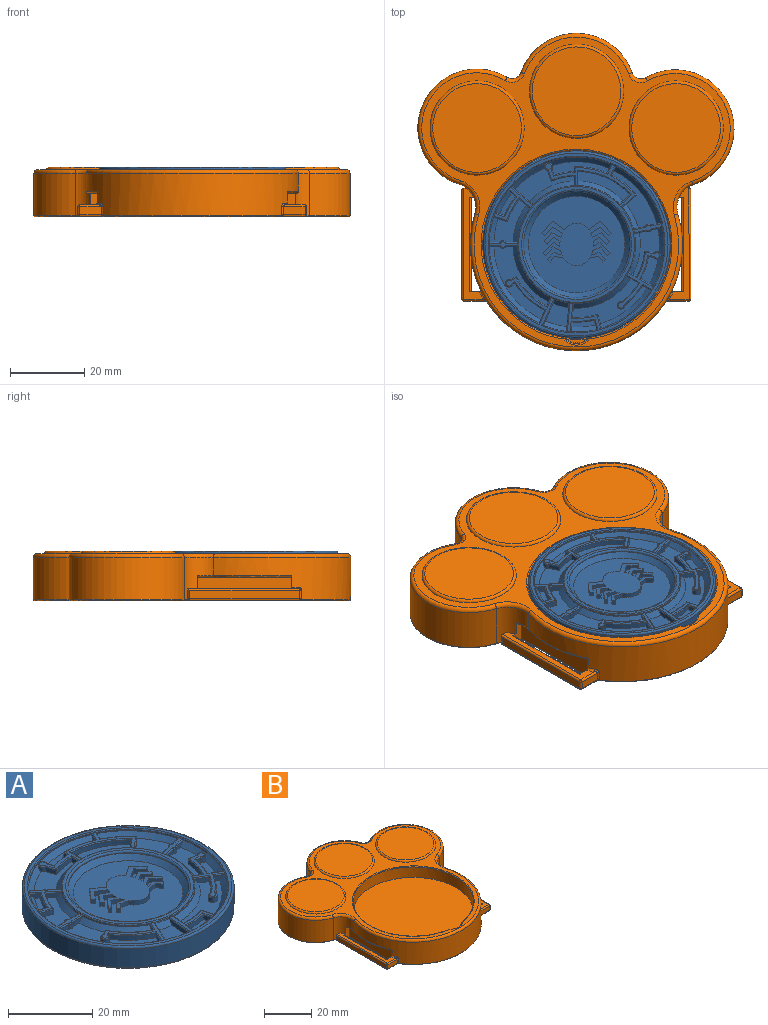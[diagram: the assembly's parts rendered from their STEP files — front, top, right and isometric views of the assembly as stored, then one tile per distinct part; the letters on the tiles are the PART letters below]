
ASSEMBLY  parts=2 mates=1
PART A: 221 faces, bbox 54.4x54.4x6.4 mm
  f0: plane 7.35x4.62mm, normal (0,0,1), area 17.8mm2, adj f80,f81,f82,f83,f107
  f1: plane 15.54x3.59mm, normal (0,0,1), area 28.4mm2, adj f25,f26,f27,f28,f29,f30,f109
  f2: cylinder r=15.88mm len=31.75mm, axis (0,0,-1), area 35mm2, adj f21,f22,f33,f34,f35,f37,f38,f43
  f3: plane 20.12x12.27mm, normal (0,0,1), area 78.1mm2, adj f48,f49,f50,f75,f76,f77,f78,f79
  f4: plane 15.52x12.18mm, normal (0,0,1), area 55.7mm2, adj f22,f23,f24,f71,f72,f73,f99,f108
  f5: plane 19.5x14.78mm, normal (0,0,1), area 91.8mm2, adj f52,f53,f54,f55,f56,f57,f58,f64
  f6: plane 6.29x6.24mm, normal (0,0,1), area 26.9mm2, adj f44,f59,f93,f103
  f7: plane 12.99x7.16mm, normal (0,0,1), area 38mm2, adj f68,f69,f70,f83,f84,f85,f86,f98
  f8: plane 11.56x8.8mm, normal (0,0,1), area 45mm2, adj f36,f37,f42,f61,f62,f63,f95,f105
  f9: plane 6.13x4.32mm, normal (0,0,1), area 8.6mm2, adj f39,f40,f41,f106
  f10: plane 6.52x1.92mm, normal (0,0,1), area 8.6mm2, adj f45,f46,f47,f102
  f11: plane 16.01x9.07mm, normal (0,0,1), area 54.4mm2, adj f30,f31,f32,f33,f38,f96,f109
  f12: cylinder r=25.15mm len=50.29mm, axis (0,0,1), area 872.9mm2, adj f88,f171
  f13: plane 49.66x49.66mm, normal (0,0,-1), area 1936.6mm2, adj f171
  f14: cylinder r=23.58mm len=47.17mm, axis (0,0,-1), area 53.1mm2, adj f24,f25,f35,f38,f39,f41,f42,f43
  f15: plane 49.28x49.28mm, normal (0,0,1), area 121.8mm2, adj f88,f90
  f16: plane 13.76x7.93mm, normal (0,0,1), area 36.7mm2, adj f20,f21,f34,f100
  f17: cylinder r=14.29mm len=28.58mm, axis (0,0,-1), area 11.4mm2, adj f89,f92
  f18: plane 31.24x31.24mm, normal (0,0,1), area 78.9mm2, adj f89,f91
  f19: plane 26.04x26.04mm, normal (0,0,1), area 405.4mm2, adj f92,f172,f173,f174,f175,f176,f177,f178
  f20: cylinder r=19.69mm len=13.76mm, axis (0,0,-1), area 20.7mm2, adj f16,f21,f34,f111
  f21: plane 2.85x2.53mm, normal (-0.66,0.75,0), area 4.3mm2, adj f2,f16,f20,f100,f112
  f22: plane 3.83x3.35mm, normal (0.66,-0.75,0), area 6mm2, adj f2,f4,f23,f99,f115
  f23: cylinder r=20.96mm len=6.76mm, axis (0,0,-1), area 11.6mm2, adj f4,f22,f24,f114
  f24: plane 2.38x1.33mm, normal (0.91,-0.42,0), area 2.7mm2, adj f4,f14,f23,f108,f113
  f25: plane 2.39x1.33mm, normal (-0.91,0.42,0), area 2.7mm2, adj f1,f14,f26,f109,f124
  f26: cylinder r=20.96mm len=8.91mm, axis (0,0,-1), area 12.2mm2, adj f1,f25,f27,f123
  f27: plane 1.33x1.27mm, normal (-1,0,0), area 1.7mm2, adj f1,f26,f28,f122
  f28: cylinder r=19.69mm len=5.45mm, axis (0,0,-1), area 7.4mm2, adj f1,f27,f29,f121
  f29: plane 1.66x1.33mm, normal (0.94,0.34,0), area 2.4mm2, adj f1,f28,f30,f120
  f30: cylinder r=1.07mm len=2.13mm, axis (0,0,-1), area 4.9mm2, adj f1,f11,f29,f31,f109,f119
  f31: plane 2.85x1.33mm, normal (-0.94,-0.34,0), area 4mm2, adj f11,f30,f32,f118
  f32: cylinder r=18.41mm len=6.22mm, axis (0,0,-1), area 8.5mm2, adj f11,f31,f33,f117
  f33: plane 2.54x1.34mm, normal (-1,0,0), area 2.6mm2, adj f2,f11,f32,f96,f116
  f34: plane 3.81x1.34mm, normal (1,0,0), area 4.3mm2, adj f2,f16,f20,f100,f110
  f35: plane 24.22x11.62mm, normal (0,0,1), area 30.8mm2, adj f2,f14,f110,f111,f112,f113,f114,f115
  f36: cylinder r=19.69mm len=6.06mm, axis (0,0,-1), area 9.2mm2, adj f8,f37,f42,f165
  f37: plane 2.92x2.46mm, normal (-0.64,-0.77,0), area 4.3mm2, adj f2,f8,f36,f95,f166
  f38: plane 5.9x4.97mm, normal (0.64,0.76,0), area 8.7mm2, adj f2,f11,f14,f96,f109,f167
  f39: plane 2.01x1.7mm, normal (-0.64,-0.76,0), area 2.7mm2, adj f9,f14,f40,f106,f170
  f40: cylinder r=20.96mm len=5.25mm, axis (0,0,-1), area 8.1mm2, adj f9,f39,f41,f169
  f41: plane 2.47x1.33mm, normal (0.34,0.94,0), area 2.7mm2, adj f9,f14,f40,f106,f168
  f42: plane 3.67x1.34mm, normal (-0.34,-0.94,0), area 4.4mm2, adj f8,f14,f36,f105,f164
  f43: plane 10.4x9.03mm, normal (0,0,1), area 13.5mm2, adj f2,f14,f164,f165,f166,f167,f168,f169
  f44: plane 7.68x1.34mm, normal (-1,0.09,0), area 8.7mm2, adj f2,f6,f14,f93,f103,f149
  f45: plane 2.62x1.33mm, normal (1,-0.09,0), area 2.7mm2, adj f10,f14,f46,f102,f145
  f46: cylinder r=20.96mm len=6.04mm, axis (0,0,-1), area 8.1mm2, adj f10,f45,f47,f144
  f47: plane 2.54x1.33mm, normal (-0.97,-0.26,0), area 2.7mm2, adj f10,f14,f46,f102,f143
  f48: plane 3.77x1.33mm, normal (0.97,0.26,0), area 4.4mm2, adj f3,f14,f49,f101,f148
  f49: cylinder r=19.69mm len=6.83mm, axis (0,0,-1), area 9.2mm2, adj f3,f48,f50,f147
  f50: plane 3.8x1.34mm, normal (1,-0.09,0), area 4.3mm2, adj f2,f3,f49,f97,f146
  f51: plane 8.95x7.75mm, normal (0,0,1), area 13.5mm2, adj f2,f14,f143,f144,f145,f146,f147,f148
  f52: plane 2.33x1.34mm, normal (-0.91,0.41,0), area 2.6mm2, adj f2,f5,f53,f94,f155
  f53: cylinder r=18.41mm len=8.22mm, axis (0,0,-1), area 15.5mm2, adj f5,f52,f54,f156
  f54: plane 1.51x1.33mm, normal (-0.5,0.87,0), area 2.3mm2, adj f5,f53,f55,f154
  f55: cylinder r=1.02mm len=2.03mm, axis (0,0,-1), area 6.7mm2, adj f5,f54,f56,f153
  f56: plane 1.33x0.41mm, normal (0.5,-0.87,0), area 0.6mm2, adj f5,f55,f57,f152
  f57: cylinder r=19.69mm len=8.17mm, axis (0,0,-1), area 14.8mm2, adj f5,f56,f58,f151
  f58: plane 3.57x1.58mm, normal (-0.91,0.41,0), area 4.4mm2, adj f5,f14,f57,f104,f150
  f59: plane 7.05x3.13mm, normal (0.91,-0.41,0), area 8.7mm2, adj f2,f6,f14,f93,f103,f157
  f60: plane 12.82x12.71mm, normal (0,0,1), area 17.4mm2, adj f2,f14,f150,f151,f152,f153,f154,f155
  f61: plane 3.23x1.34mm, normal (0,1,0), area 3.5mm2, adj f2,f8,f62,f95,f161
  f62: cylinder r=1.02mm len=1.59mm, axis (0,0,-1), area 2.4mm2, adj f8,f61,f63,f162
  f63: plane 2.9x1.33mm, normal (0,1,0), area 3.1mm2, adj f8,f14,f62,f105,f163
  f64: plane 2.9x1.33mm, normal (0,-1,0), area 3.1mm2, adj f5,f14,f65,f104,f158
  f65: cylinder r=1.02mm len=1.59mm, axis (0,0,-1), area 2.4mm2, adj f5,f64,f66,f160
  f66: plane 3.23x1.34mm, normal (0,-1,0), area 3.5mm2, adj f2,f5,f65,f94,f159
  f67: plane 7.71x1.52mm, normal (0,0,1), area 6.6mm2, adj f2,f14,f158,f159,f160,f161,f162,f163
  f68: plane 3.15x1.34mm, normal (0.22,-0.97,0), area 3.5mm2, adj f2,f7,f69,f98,f127
  f69: cylinder r=1.02mm len=1.55mm, axis (0,0,-1), area 2.4mm2, adj f7,f68,f70,f126
  f70: plane 2.83x1.33mm, normal (0.22,-0.97,0), area 3.1mm2, adj f7,f14,f69,f107,f125
  f71: plane 2.83x1.33mm, normal (-0.22,0.97,0), area 3.1mm2, adj f4,f14,f72,f108,f130
  f72: cylinder r=1.02mm len=1.55mm, axis (0,0,-1), area 2.4mm2, adj f4,f71,f73,f129
  f73: plane 3.15x1.34mm, normal (-0.22,0.97,0), area 3.5mm2, adj f2,f4,f72,f99,f128
  f74: plane 7.69x2.46mm, normal (0,0,1), area 6.6mm2, adj f2,f14,f125,f126,f127,f128,f129,f130
  f75: plane 3.3x1.92mm, normal (-0.5,-0.86,0), area 4.3mm2, adj f2,f3,f76,f97,f135
  f76: cylinder r=19.69mm len=5mm, axis (0,0,-1), area 9mm2, adj f3,f75,f77,f134
  f77: cylinder r=1.02mm len=2.03mm, axis (0,0,-1), area 6.7mm2, adj f3,f76,f78,f133
  f78: cylinder r=20.96mm len=5.38mm, axis (0,0,-1), area 9.6mm2, adj f3,f77,f79,f132
  f79: plane 2.28x1.33mm, normal (-0.5,-0.87,0), area 2.7mm2, adj f3,f14,f78,f101,f131
  f80: plane 3.38x1.95mm, normal (0.5,0.87,0), area 4.4mm2, adj f0,f14,f81,f107,f142
  f81: cylinder r=19.69mm len=6.03mm, axis (0,0,-1), area 8.5mm2, adj f0,f80,f82,f141
  f82: plane 1.36x1.33mm, normal (-0.13,-0.99,0), area 1.8mm2, adj f0,f81,f83,f140
  f83: cylinder r=1.02mm len=2.03mm, axis (0,0,-1), area 5.9mm2, adj f0,f7,f82,f84,f107,f139
  f84: plane 2.62x1.33mm, normal (0.13,0.99,0), area 3.5mm2, adj f7,f83,f85,f138
  f85: cylinder r=18.41mm len=6.82mm, axis (0,0,-1), area 9.6mm2, adj f7,f84,f86,f137
  f86: plane 2.2x1.34mm, normal (0.5,0.87,0), area 2.6mm2, adj f2,f7,f85,f98,f136
  f87: plane 15.02x11.14mm, normal (0,0,1), area 22mm2, adj f2,f14,f131,f132,f133,f134,f135,f136
  f88: torus R=24.64mm, axis (0,0,1), area 125.2mm2, adj f12,f15
  f89: torus R=14.8mm, axis (0,0,1), area 72.6mm2, adj f17,f18
  f90: torus R=23.84mm, axis (0,0,1), area 59.4mm2, adj f14,f15
  f91: torus R=15.62mm, axis (0,0,1), area 39.6mm2, adj f2,f18
  f92: cone r=14.29mm half-angle=45deg, axis (0,0,1), area 154.1mm2, adj f17,f19
  f93: cone r=15.88mm half-angle=45deg, axis (0,0,-1), area 7.4mm2, adj f2,f6,f44,f59
  f94: cone r=15.88mm half-angle=45deg, axis (0,0,-1), area 31.9mm2, adj f2,f5,f52,f66
  f95: cone r=15.88mm half-angle=45deg, axis (0,0,-1), area 18.5mm2, adj f2,f8,f37,f61
  f96: cone r=15.88mm half-angle=45deg, axis (0,0,-1), area 23.5mm2, adj f2,f11,f33,f38
  f97: cone r=15.88mm half-angle=45deg, axis (0,0,-1), area 31.4mm2, adj f2,f3,f50,f75
  f98: cone r=15.88mm half-angle=45deg, axis (0,0,-1), area 19.9mm2, adj f2,f7,f68,f86
  f99: cone r=15.88mm half-angle=45deg, axis (0,0,-1), area 12.4mm2, adj f2,f4,f22,f73
  f100: cone r=15.88mm half-angle=45deg, axis (0,0,-1), area 23mm2, adj f2,f16,f21,f34
  f101: cone r=22.31mm half-angle=45deg, axis (0,0,1), area 30.1mm2, adj f3,f14,f48,f79
  f102: cone r=22.31mm half-angle=45deg, axis (0,0,1), area 12.2mm2, adj f10,f14,f45,f47
  f103: cone r=22.31mm half-angle=45deg, axis (0,0,1), area 11.2mm2, adj f6,f14,f44,f59
  f104: cone r=22.31mm half-angle=45deg, axis (0,0,1), area 45.3mm2, adj f5,f14,f58,f64
  f105: cone r=22.31mm half-angle=45deg, axis (0,0,1), area 12.1mm2, adj f8,f14,f42,f63
  f106: cone r=22.31mm half-angle=45deg, axis (0,0,1), area 12.2mm2, adj f9,f14,f39,f41
  f107: cone r=22.31mm half-angle=45deg, axis (0,0,1), area 27.5mm2, adj f0,f7,f14,f70,f80,f83
  f108: cone r=22.31mm half-angle=45deg, axis (0,0,1), area 35.2mm2, adj f4,f14,f24,f71
  f109: cone r=22.31mm half-angle=45deg, axis (0,0,1), area 49.1mm2, adj f1,f11,f14,f25,f30,f38
  f110: cylinder r=0.25mm len=4.07mm, axis (0,-1,0), area 1.6mm2, adj f2,f34,f35,f111
  f111: torus R=19.94mm, axis (0,0,1), area 6.3mm2, adj f20,f35,f110,f112
  f112: cylinder r=0.25mm len=3.22mm, axis (0.75,0.66,0), area 1.6mm2, adj f2,f21,f35,f111
  f113: cylinder r=0.25mm len=2.72mm, axis (-0.42,-0.91,0), area 1.1mm2, adj f14,f24,f35,f114
  f114: torus R=20.7mm, axis (0,0,1), area 3.5mm2, adj f23,f35,f113,f115
  f115: cylinder r=0.25mm len=3.99mm, axis (-0.75,-0.66,0), area 2mm2, adj f2,f22,f35,f114
  f116: cylinder r=0.25mm len=2.8mm, axis (0,1,0), area 1.1mm2, adj f2,f33,f35,f117
  f117: torus R=18.67mm, axis (0,0,1), area 2.6mm2, adj f32,f35,f116,f118
  f118: cylinder r=0.25mm len=3.07mm, axis (-0.34,0.94,0), area 1.2mm2, adj f31,f35,f117,f119
  f119: torus R=0.81mm, axis (0,0,1), area 2mm2, adj f30,f35,f118,f120
  f120: cylinder r=0.25mm len=2.11mm, axis (0.34,-0.94,0), area 0.8mm2, adj f29,f35,f119,f121
  f121: torus R=19.43mm, axis (0,0,1), area 2.3mm2, adj f28,f35,f120,f122
  f122: cylinder r=0.25mm len=1.52mm, axis (0,1,0), area 0.5mm2, adj f27,f35,f121,f123
  f123: torus R=20.7mm, axis (0,0,1), area 3.6mm2, adj f26,f35,f122,f124
  f124: cylinder r=0.25mm len=2.72mm, axis (0.42,0.91,0), area 1.1mm2, adj f14,f25,f35,f123
  f125: cylinder r=0.25mm len=3.02mm, axis (-0.97,-0.22,0), area 1.2mm2, adj f14,f70,f74,f126
  f126: torus R=0.76mm, axis (0,0,1), area 0.7mm2, adj f69,f74,f125,f127
  f127: cylinder r=0.25mm len=3.33mm, axis (-0.97,-0.22,0), area 1.3mm2, adj f2,f68,f74,f126
  f128: cylinder r=0.25mm len=3.33mm, axis (0.97,0.22,0), area 1.3mm2, adj f2,f73,f74,f129
  f129: torus R=0.76mm, axis (0,0,1), area 0.7mm2, adj f72,f74,f128,f130
  f130: cylinder r=0.25mm len=3.02mm, axis (0.97,0.22,0), area 1.2mm2, adj f14,f71,f74,f129
  f131: cylinder r=0.25mm len=2.62mm, axis (-0.87,0.5,0), area 1.1mm2, adj f14,f79,f87,f132
  f132: torus R=20.7mm, axis (0,0,1), area 2.9mm2, adj f78,f87,f131,f133
  f133: torus R=0.76mm, axis (0,0,1), area 1.9mm2, adj f77,f87,f132,f134
  f134: torus R=19.94mm, axis (0,0,1), area 2.8mm2, adj f76,f87,f133,f135
  f135: cylinder r=0.25mm len=3.65mm, axis (-0.86,0.5,0), area 1.6mm2, adj f2,f75,f87,f134
  f136: cylinder r=0.25mm len=2.55mm, axis (0.87,-0.5,0), area 1.1mm2, adj f2,f86,f87,f137
  f137: torus R=18.67mm, axis (0,0,1), area 2.9mm2, adj f85,f87,f136,f138
  f138: cylinder r=0.25mm len=2.79mm, axis (0.99,-0.13,0), area 1mm2, adj f84,f87,f137,f139
  f139: torus R=0.76mm, axis (0,0,1), area 1.9mm2, adj f83,f87,f138,f140
  f140: cylinder r=0.25mm len=1.77mm, axis (-0.99,0.13,0), area 0.6mm2, adj f82,f87,f139,f141
  f141: torus R=19.43mm, axis (0,0,1), area 2.6mm2, adj f81,f87,f140,f142
  f142: cylinder r=0.25mm len=3.72mm, axis (0.87,-0.5,0), area 1.6mm2, adj f14,f80,f87,f141
  f143: cylinder r=0.25mm len=2.85mm, axis (-0.26,0.97,0), area 1.1mm2, adj f14,f47,f51,f144
  f144: torus R=20.7mm, axis (0,0,1), area 2.5mm2, adj f46,f51,f143,f145
  f145: cylinder r=0.25mm len=2.89mm, axis (-0.09,-1,0), area 1.1mm2, adj f14,f45,f51,f144
  f146: cylinder r=0.25mm len=4.08mm, axis (-0.09,-1,0), area 1.6mm2, adj f2,f50,f51,f147
  f147: torus R=19.94mm, axis (0,0,1), area 2.8mm2, adj f49,f51,f146,f148
  f148: cylinder r=0.25mm len=3.84mm, axis (0.26,-0.97,0), area 1.5mm2, adj f14,f48,f51,f147
  f149: cylinder r=0.25mm len=7.71mm, axis (0.09,1,0), area 3.1mm2, adj f2,f14,f44,f51
  f150: cylinder r=0.25mm len=3.9mm, axis (0.41,0.91,0), area 1.6mm2, adj f14,f58,f60,f151
  f151: torus R=19.43mm, axis (0,0,1), area 4.5mm2, adj f57,f60,f150,f152
  f152: cylinder r=0.25mm len=0.87mm, axis (-0.87,-0.5,0), area 0.3mm2, adj f56,f60,f151,f153
  f153: torus R=0.76mm, axis (0,0,1), area 1.9mm2, adj f55,f60,f152,f154
  f154: cylinder r=0.25mm len=1.76mm, axis (0.87,0.5,0), area 0.7mm2, adj f54,f60,f153,f156
  f155: cylinder r=0.25mm len=2.67mm, axis (0.41,0.91,0), area 1.1mm2, adj f2,f52,f60,f156
  f156: torus R=18.67mm, axis (0,0,1), area 4.7mm2, adj f53,f60,f154,f155
  f157: cylinder r=0.25mm len=7.16mm, axis (-0.41,-0.91,0), area 3.1mm2, adj f2,f14,f59,f60
  f158: cylinder r=0.25mm len=3.04mm, axis (-1,0,0), area 1.2mm2, adj f14,f64,f67,f160
  f159: cylinder r=0.25mm len=3.36mm, axis (-1,0,0), area 1.3mm2, adj f2,f66,f67,f160
  f160: torus R=0.76mm, axis (0,0,1), area 0.7mm2, adj f65,f67,f158,f159
  f161: cylinder r=0.25mm len=3.36mm, axis (1,0,0), area 1.3mm2, adj f2,f61,f67,f162
  f162: torus R=0.76mm, axis (0,0,1), area 0.7mm2, adj f62,f67,f161,f163
  f163: cylinder r=0.25mm len=3.04mm, axis (1,0,0), area 1.2mm2, adj f14,f63,f67,f162
  f164: cylinder r=0.25mm len=3.76mm, axis (-0.94,0.34,0), area 1.5mm2, adj f14,f42,f43,f165
  f165: torus R=19.94mm, axis (0,0,1), area 2.8mm2, adj f36,f43,f164,f166
  f166: cylinder r=0.25mm len=3.28mm, axis (-0.77,0.64,0), area 1.6mm2, adj f2,f37,f43,f165
  f167: cylinder r=0.25mm len=6.07mm, axis (0.76,-0.64,0), area 3.1mm2, adj f2,f14,f38,f43
  f168: cylinder r=0.25mm len=2.8mm, axis (0.94,-0.34,0), area 1.1mm2, adj f14,f41,f43,f169
  f169: torus R=20.7mm, axis (0,0,1), area 2.5mm2, adj f40,f43,f168,f170
  f170: cylinder r=0.25mm len=2.37mm, axis (-0.76,0.64,0), area 1.1mm2, adj f14,f39,f43,f169
  f171: torus R=24.83mm, axis (0,0,1), area 78.4mm2, adj f12,f13
  f172: plane 1.2x0.71mm, normal (0.68,-0.73,0), area 1.2mm2, adj f19,f173,f219,f220
  f173: plane 1.88x1.75mm, normal (0.73,0.68,0), area 3.1mm2, adj f19,f172,f174,f220
  f174: plane 2.15x1.2mm, normal (-0.29,0.96,0), area 2.7mm2, adj f19,f173,f175,f220
  f175: extruded ~1.2x1.09mm, area 1.4mm2, adj f19,f174,f176,f220
  f176: plane 2.07x1.2mm, normal (0.48,-0.88,0), area 2.8mm2, adj f19,f175,f177,f220
  f177: plane 2.37x2.03mm, normal (-0.76,-0.65,0), area 3.7mm2, adj f19,f176,f178,f220
  f178: plane 1.2x0.62mm, normal (0.65,-0.76,0), area 1mm2, adj f19,f177,f179,f220
  f179: plane 3.13x2.68mm, normal (0.76,0.65,0), area 4.9mm2, adj f19,f178,f180,f220
  f180: plane 1.86x1.23mm, normal (-0.55,0.83,0), area 2.7mm2, adj f19,f179,f181,f220
  f181: extruded ~1.41x1.2mm, area 1.7mm2, adj f19,f180,f182,f220
  f182: plane 1.78x1.2mm, normal (0.55,-0.84,0), area 2.6mm2, adj f19,f181,f183,f220
  f183: plane 2x1.71mm, normal (-0.76,-0.65,0), area 3.2mm2, adj f19,f182,f184,f220
  f184: plane 1.2x0.81mm, normal (0.65,-0.76,0), area 1.3mm2, adj f19,f183,f185,f220
  f185: plane 2.46x2.1mm, normal (0.76,0.65,0), area 3.9mm2, adj f19,f184,f186,f220
  f186: plane 2.42x1.23mm, normal (-0.45,0.89,0), area 3.3mm2, adj f19,f185,f187,f220
  f187: extruded ~1.2x1.06mm, area 1.4mm2, adj f19,f186,f188,f220
  f188: plane 2.72x1.74mm, normal (0.54,-0.84,0), area 3.9mm2, adj f19,f187,f189,f220
  f189: plane 2.37x2.03mm, normal (-0.76,-0.65,0), area 3.7mm2, adj f19,f188,f190,f220
  f190: plane 1.2x0.79mm, normal (0.65,-0.76,0), area 1.2mm2, adj f19,f189,f191,f220
  f191: plane 3.29x2.82mm, normal (0.76,0.65,0), area 5.2mm2, adj f19,f190,f192,f220
  f192: plane 3.33x2.32mm, normal (-0.57,0.82,0), area 4.9mm2, adj f19,f191,f193,f220
  f193: extruded ~6.5x1.76mm, area 9.2mm2, adj f19,f192,f194,f220
  f194: plane 3.33x2.32mm, normal (0.57,0.82,0), area 4.9mm2, adj f19,f193,f195,f220
  f195: plane 3.29x2.82mm, normal (-0.76,0.65,0), area 5.2mm2, adj f19,f194,f196,f220
  f196: plane 1.2x0.79mm, normal (-0.65,-0.76,0), area 1.2mm2, adj f19,f195,f197,f220
  f197: plane 2.37x2.03mm, normal (0.76,-0.65,0), area 3.7mm2, adj f19,f196,f198,f220
  f198: plane 2.72x1.74mm, normal (-0.54,-0.84,0), area 3.9mm2, adj f19,f197,f199,f220
  f199: extruded ~1.2x1.06mm, area 1.4mm2, adj f19,f198,f200,f220
  f200: plane 2.42x1.23mm, normal (0.45,0.89,0), area 3.3mm2, adj f19,f199,f201,f220
  f201: plane 2.46x2.1mm, normal (-0.76,0.65,0), area 3.9mm2, adj f19,f200,f202,f220
  f202: plane 1.2x0.81mm, normal (-0.65,-0.76,0), area 1.3mm2, adj f19,f201,f203,f220
  f203: plane 2x1.71mm, normal (0.76,-0.65,0), area 3.2mm2, adj f19,f202,f204,f220
  f204: plane 1.78x1.2mm, normal (-0.55,-0.84,0), area 2.6mm2, adj f19,f203,f205,f220
  f205: extruded ~1.41x1.2mm, area 1.7mm2, adj f19,f204,f206,f220
  f206: plane 1.86x1.23mm, normal (0.55,0.83,0), area 2.7mm2, adj f19,f205,f207,f220
  f207: plane 3.13x2.68mm, normal (-0.76,0.65,0), area 4.9mm2, adj f19,f206,f208,f220
  f208: plane 1.2x0.62mm, normal (-0.65,-0.76,0), area 1mm2, adj f19,f207,f209,f220
  f209: plane 2.37x2.03mm, normal (0.76,-0.65,0), area 3.7mm2, adj f19,f208,f210,f220
  f210: plane 2.07x1.2mm, normal (-0.48,-0.88,0), area 2.8mm2, adj f19,f209,f211,f220
  f211: extruded ~1.2x1.09mm, area 1.4mm2, adj f19,f210,f212,f220
  f212: plane 2.15x1.2mm, normal (0.29,0.96,0), area 2.7mm2, adj f19,f211,f213,f220
  f213: plane 1.88x1.75mm, normal (-0.73,0.68,0), area 3.1mm2, adj f19,f212,f214,f220
  f214: plane 1.2x0.71mm, normal (-0.68,-0.73,0), area 1.2mm2, adj f19,f213,f215,f220
  f215: plane 1.55x1.2mm, normal (0.8,-0.6,0), area 2.3mm2, adj f19,f214,f216,f220
  f216: plane 2.46x1.2mm, normal (-0.19,-0.98,0), area 3mm2, adj f19,f215,f217,f220
  f217: extruded ~6.96x2.09mm, area 10.2mm2, adj f19,f216,f218,f220
  f218: plane 2.46x1.2mm, normal (0.19,-0.98,0), area 3mm2, adj f19,f217,f219,f220
  f219: plane 1.55x1.2mm, normal (-0.8,-0.6,0), area 2.3mm2, adj f19,f172,f218,f220
  f220: plane 18.78x12.04mm, normal (0,0,1), area 127mm2, adj f172,f173,f174,f175,f176,f177,f178,f179
PART B: 108 faces, bbox 87.9x89.3x13.4 mm
  f0: plane 85.03x84.66mm, normal (0,0,-1), area 4711.8mm2, adj f3,f4,f40,f41,f42,f43,f44,f45
  f1: cylinder r=28.57mm len=57.15mm, axis (0,0,1), area 913mm2, adj f2,f3,f21,f22,f49,f59,f65,f67
  f2: cylinder r=6.35mm len=11.43mm, axis (0,0,-1), area 72.4mm2, adj f1,f4,f8,f23,f46,f47,f48,f66
  f3: torus R=28.32mm, axis (0,0,1), area 23mm2, adj f0,f1,f93,f105
  f4: torus R=6.6mm, axis (0,0,1), area 1mm2, adj f0,f2,f45,f79
  f5: cylinder r=25.4mm len=50.8mm, axis (0,0,-1), area 838.1mm2, adj f13,f30,f31,f33,f36,f37,f39
  f6: cylinder r=15.88mm len=29.94mm, axis (0,0,1), area 447mm2, adj f19,f20,f29,f41
  f7: cylinder r=15.88mm len=31.04mm, axis (0,0,1), area 613.6mm2, adj f19,f21,f26,f42
  f8: cylinder r=15.88mm len=30.98mm, axis (0,0,1), area 608.4mm2, adj f2,f20,f25,f45
  f9: plane 83.51x83.14mm, normal (0,0,1), area 927mm2, adj f16,f17,f18,f22,f23,f24,f25,f26
  f10: plane 23.9x23.9mm, normal (0,0,1), area 448.5mm2, adj f17
  f11: plane 23.9x23.9mm, normal (0,0,1), area 448.5mm2, adj f16
  f12: plane 23.9x23.9mm, normal (0,0,1), area 448.5mm2, adj f18
  f13: plane 50.8x50.8mm, normal (0,0,1), area 2026.8mm2, adj f5
  f14: cylinder r=4.76mm len=7.02mm, axis (0,0,1), area 20mm2, adj f30,f34,f35,f39
  f15: plane 5.29x0.87mm, normal (0,0,1), area 2.7mm2, adj f33,f34
  f16: torus R=11.95mm, axis (0,0,-1), area 83.3mm2, adj f9,f11
  f17: torus R=11.95mm, axis (0,0,-1), area 83.3mm2, adj f9,f10
  f18: torus R=11.95mm, axis (0,0,-1), area 83.3mm2, adj f9,f12
  f19: cylinder r=2.54mm len=11.43mm, axis (0,0,-1), area 51.4mm2, adj f6,f7,f28,f40
  f20: cylinder r=2.54mm len=11.43mm, axis (0,0,-1), area 51mm2, adj f6,f8,f27,f43
  f21: cylinder r=6.35mm len=11.43mm, axis (0,0,-1), area 74.7mm2, adj f1,f7,f24,f44,f53,f54,f55,f64
  f22: torus R=27.56mm, axis (0,0,1), area 168mm2, adj f1,f9,f23,f24
  f23: torus R=7.37mm, axis (0,0,1), area 16.6mm2, adj f2,f9,f22,f25
  f24: torus R=7.37mm, axis (0,0,1), area 16.8mm2, adj f9,f21,f22,f26
  f25: torus R=14.86mm, axis (0,0,1), area 83mm2, adj f8,f9,f23,f27
  f26: torus R=14.86mm, axis (0,0,1), area 83.7mm2, adj f7,f9,f24,f28
  f27: torus R=3.56mm, axis (0,0,1), area 8.2mm2, adj f9,f20,f25,f29
  f28: torus R=3.56mm, axis (0,0,1), area 8.2mm2, adj f9,f19,f26,f29
  f29: torus R=14.86mm, axis (0,0,1), area 61mm2, adj f6,f9,f27,f28
  f30: cylinder r=0.32mm len=2.54mm, axis (0,0,1), area 0.6mm2, adj f5,f14,f31,f32
  f31: bspline ~1.74x0.69mm, area 0.4mm2, adj f5,f30,f33,f34
  f32: sphere r=0.32mm, area 0.1mm2, adj f30,f35,f36
  f33: torus R=25.72mm, axis (0,0,1), area 2.6mm2, adj f5,f15,f31,f37
  f34: torus R=4.45mm, axis (0,0,1), area 3.5mm2, adj f14,f15,f31,f37
  f35: torus R=5.08mm, axis (0,0,1), area 4mm2, adj f9,f14,f32,f38
  f36: torus R=25.72mm, axis (0,0,1), area 76.2mm2, adj f5,f9,f32,f38
  f37: bspline ~1.21x0.74mm, area 0.4mm2, adj f5,f33,f34,f39
  f38: sphere r=0.32mm, area 0.1mm2, adj f35,f36,f39
  f39: cylinder r=0.32mm len=2.54mm, axis (0,0,1), area 0.6mm2, adj f5,f14,f37,f38
  f40: torus R=2.79mm, axis (0,0,1), area 1.9mm2, adj f0,f19,f41,f42
  f41: torus R=15.62mm, axis (0,0,1), area 15.5mm2, adj f0,f6,f40,f43
  f42: torus R=15.62mm, axis (0,0,1), area 21.3mm2, adj f0,f7,f40,f44
  f43: torus R=2.79mm, axis (0,0,1), area 1.8mm2, adj f0,f20,f41,f45
  f44: torus R=6.6mm, axis (0,0,1), area 1.1mm2, adj f0,f21,f42,f76
  f45: torus R=15.62mm, axis (0,0,1), area 21.1mm2, adj f0,f4,f8,f43
  f46: plane 29.98x5.26mm, normal (0,0,1), area 53.2mm2, adj f2,f47,f48,f49,f97,f100,f101,f107
  f47: plane 6.43x3.55mm, normal (0,-1,0), area 15.4mm2, adj f2,f46,f50,f60,f61,f66,f69,f107
  f48: plane 2.67x0.53mm, normal (0,1,0), area 1.4mm2, adj f2,f46,f79,f95,f97
  f49: plane 6.45x3.57mm, normal (0,1,0), area 9mm2, adj f1,f46,f50,f60,f67,f70,f100,f107
  f50: plane 25.4x2.16mm, normal (-1,0,0), area 54.8mm2, adj f47,f49,f68,f107
  f51: plane 29.47x2.16mm, normal (1,0,0), area 63.6mm2, adj f81,f95,f97,f98
  f52: plane 5.89x2.16mm, normal (0,-1,0), area 12.7mm2, adj f80,f98,f101,f103
  f53: plane 29.97x5.24mm, normal (0,0,1), area 53.2mm2, adj f21,f54,f55,f59,f86,f88,f89,f106
  f54: plane 2.67x0.79mm, normal (0,1,0), area 2.1mm2, adj f21,f53,f76,f84
  f55: plane 6.43x3.56mm, normal (0,-1,0), area 15.1mm2, adj f21,f53,f58,f62,f63,f64,f73,f106
  f56: plane 5.86x2.16mm, normal (0,-1,0), area 12.7mm2, adj f77,f85,f88,f91
  f57: plane 29.46x2.16mm, normal (-1,0,0), area 63.6mm2, adj f78,f84,f85,f86
  f58: plane 25.4x2.16mm, normal (1,0,0), area 54.8mm2, adj f55,f59,f72,f106
  f59: plane 6.45x3.58mm, normal (0,1,0), area 9mm2, adj f1,f53,f58,f62,f65,f74,f89,f106
  f60: plane 25.41x5.92mm, normal (1,0,0), area 148.4mm2, adj f47,f49,f61,f67,f71
  f61: plane 24.82x2.73mm, normal (0,0,-1), area 47.5mm2, adj f47,f60,f66,f67
  f62: plane 25.41x5.92mm, normal (-1,0,0), area 148.4mm2, adj f55,f59,f63,f65,f75
  f63: plane 24.82x2.73mm, normal (0,0,-1), area 47.3mm2, adj f55,f62,f64,f65
  f64: torus R=6.86mm, axis (0,0,-1), area 3.6mm2, adj f21,f55,f63,f65
  f65: torus R=28.07mm, axis (0,0,-1), area 17.1mm2, adj f1,f59,f62,f63,f64
  f66: torus R=6.86mm, axis (0,0,-1), area 3.7mm2, adj f2,f47,f61,f67
  f67: torus R=28.07mm, axis (0,0,-1), area 17mm2, adj f1,f49,f60,f61,f66
  f68: cylinder r=0.51mm len=26.42mm, axis (0,-1,0), area 20.6mm2, adj f0,f50,f69,f70
  f69: cylinder r=0.51mm len=3.98mm, axis (1,0,0), area 2.7mm2, adj f0,f47,f68,f71
  f70: cylinder r=0.51mm len=3.98mm, axis (-1,0,0), area 2.7mm2, adj f0,f49,f68,f71
  f71: cylinder r=0.51mm len=26.42mm, axis (0,1,0), area 20.6mm2, adj f0,f60,f69,f70
  f72: cylinder r=0.51mm len=26.42mm, axis (0,1,0), area 20.6mm2, adj f0,f58,f73,f74
  f73: cylinder r=0.51mm len=3.99mm, axis (1,0,0), area 2.7mm2, adj f0,f55,f72,f75
  f74: cylinder r=0.51mm len=3.99mm, axis (-1,0,0), area 2.7mm2, adj f0,f59,f72,f75
  f75: cylinder r=0.51mm len=26.42mm, axis (0,-1,0), area 20.6mm2, adj f0,f62,f73,f74
  f76: cylinder r=0.51mm len=1.73mm, axis (-1,0,0), area 0.9mm2, adj f0,f21,f44,f54,f82
  f77: cylinder r=0.51mm len=6.13mm, axis (1,0,0), area 4.7mm2, adj f0,f56,f83,f92,f93
  f78: cylinder r=0.51mm len=29.46mm, axis (0,-1,0), area 23.5mm2, adj f0,f57,f82,f83
  f79: cylinder r=0.51mm len=1.54mm, axis (-1,0,0), area 0.7mm2, adj f0,f2,f4,f48,f94
  f80: cylinder r=0.51mm len=6.15mm, axis (1,0,0), area 4.7mm2, adj f0,f52,f96,f104,f105
  f81: cylinder r=0.51mm len=29.47mm, axis (0,1,0), area 23.5mm2, adj f0,f51,f94,f96
  f82: sphere r=0.51mm, area 0.4mm2, adj f76,f78,f84
  f83: sphere r=0.51mm, area 0.4mm2, adj f77,f78,f85
  f84: cylinder r=0.51mm len=2.67mm, axis (0,0,1), area 2mm2, adj f54,f57,f82,f86
  f85: cylinder r=0.51mm len=2.16mm, axis (0,0,-1), area 1.7mm2, adj f56,f57,f83,f87
  f86: cylinder r=0.51mm len=29.97mm, axis (0,-1,0), area 23.8mm2, adj f53,f57,f84,f87
  f87: sphere r=0.51mm, area 0.4mm2, adj f85,f86,f88
  f88: cylinder r=0.51mm len=5.86mm, axis (1,0,0), area 4.5mm2, adj f53,f56,f87,f90
  f89: torus R=29.08mm, axis (0,0,-1), area 1.7mm2, adj f1,f53,f59,f90
  f90: bspline ~1.29x1.22mm, area 0.8mm2, adj f1,f88,f89,f91
  f91: cylinder r=0.51mm len=2.16mm, axis (0,0,1), area 1.1mm2, adj f1,f56,f90,f92
  f92: bspline ~0.51x0.5mm, area 0.1mm2, adj f1,f77,f91,f93
  f93: bspline ~0.75x0.47mm, area 0.2mm2, adj f3,f77,f92
  f94: sphere r=0.51mm, area 0.4mm2, adj f79,f81,f95
  f95: cylinder r=0.51mm len=2.67mm, axis (0,0,1), area 2mm2, adj f48,f51,f94,f97
  f96: sphere r=0.51mm, area 0.4mm2, adj f80,f81,f98
  f97: cylinder r=0.51mm len=29.98mm, axis (0,1,0), area 23.8mm2, adj f46,f48,f51,f95,f99
  f98: cylinder r=0.51mm len=2.16mm, axis (0,0,-1), area 1.7mm2, adj f51,f52,f96,f99
  f99: sphere r=0.51mm, area 0.4mm2, adj f97,f98,f101
  f100: torus R=29.08mm, axis (0,0,-1), area 1.7mm2, adj f1,f46,f49,f102
  f101: cylinder r=0.51mm len=5.89mm, axis (1,0,0), area 4.5mm2, adj f46,f52,f99,f102
  f102: bspline ~1.25x1.21mm, area 0.8mm2, adj f1,f100,f101,f103
  f103: cylinder r=0.51mm len=2.16mm, axis (0,0,1), area 1.1mm2, adj f1,f52,f102,f104
  f104: bspline ~0.51x0.46mm, area 0.1mm2, adj f1,f80,f103,f105
  f105: bspline ~0.75x0.47mm, area 0.2mm2, adj f3,f80,f104
  f106: cylinder r=0.51mm len=25.4mm, axis (0,1,0), area 20.3mm2, adj f53,f55,f58,f59
  f107: cylinder r=0.51mm len=25.4mm, axis (0,-1,0), area 20.3mm2, adj f46,f47,f49,f50
PLACE A t=(0,0,1.9)mm
PLACE B at identity
MATE parallel A.f12 <-> B.f5  axis (0,0,-1) through (0,0,-2.54)mm
